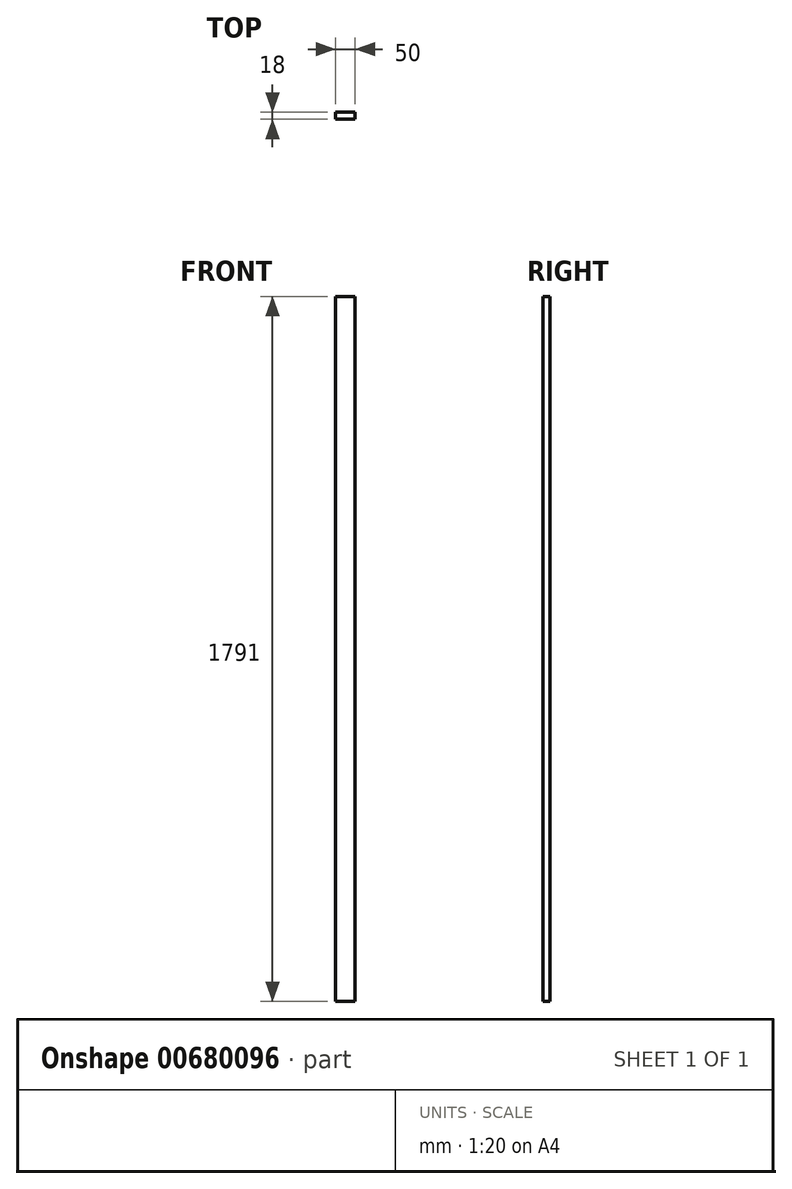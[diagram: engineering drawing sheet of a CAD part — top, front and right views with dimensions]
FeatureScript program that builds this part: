
annotation { "Feature Type Name" : "Feature", "Feature Type Description" : "" }
export const myFeature = defineFeature(function(context is Context, id is Id, definition is map)
    precondition{}
    {
        {
            var Q0;
            Q0=qCreatedBy(makeId("Front.planeOp"),FACE);
            var sketch = newSketch(context, id + "F0", { "sketchPlane" : qUnion([Q0])});
            skLineSegment(sketch, "E0.bottom", {"start": v(-25, -895.5) * mm, "end": v(25, -895.5) * mm});
            skLineSegment(sketch, "E0.top", {"start": v(-25, 895.5) * mm, "end": v(25, 895.5) * mm});
            skLineSegment(sketch, "E0.left", {"start": v(-25, -895.5) * mm, "end": v(-25, 895.5) * mm});
            skLineSegment(sketch, "E0.right", {"start": v(25, -895.5) * mm, "end": v(25, 895.5) * mm});
            skPoint(sketch, "E0.middle", {"position": v(0, 0) * mm});
            skSolve(sketch);
        }
        {
            var Q0;
            Q0=makeQuery(id+"F0.imprint","IMPRINT",FACE,{"disambiguationData":[TD([[makeQuery(id+"F0.imprint","IMPRINT",EDGE,{"derivedFrom":sQuery(id+"F0.wireOp",EDGE,"E0.bottom")}),1.0]])]});
            extrude(context, id + "F1", {"entities" : qUnion([Q0]), "endBound" : BoundingType.SYMMETRIC, "depth" : 18 * mm, "offsetDistance" : 25 * mm});
        }
    });
